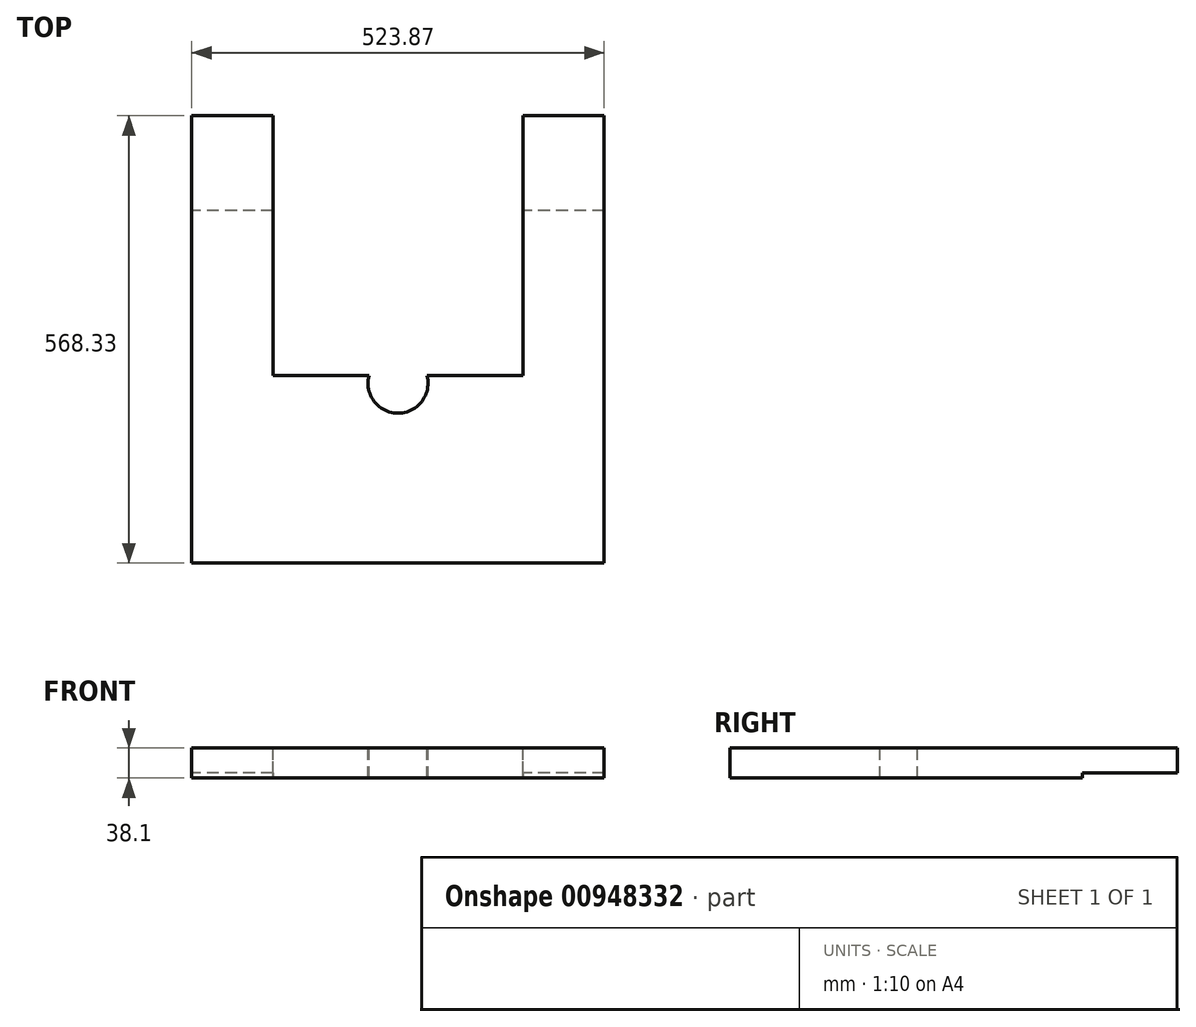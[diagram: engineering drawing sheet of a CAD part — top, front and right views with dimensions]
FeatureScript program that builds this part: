
annotation { "Feature Type Name" : "Feature", "Feature Type Description" : "" }
export const myFeature = defineFeature(function(context is Context, id is Id, definition is map)
    precondition{}
    {
        {
            var Q0;
            Q0=qCreatedBy(makeId("Top.planeOp"),FACE);
            var sketch = newSketch(context, id + "F0", { "sketchPlane" : qUnion([Q0])});
            skLineSegment(sketch, "E0.bottom", {"start": v(-267.02, 409.44) * mm, "end": v(256.85, 409.44) * mm});
            skLineSegment(sketch, "E0.top", {"start": v(-267.02, -158.89) * mm, "end": v(256.85, -158.89) * mm});
            skLineSegment(sketch, "E0.left", {"start": v(-267.02, 409.44) * mm, "end": v(-267.02, -158.89) * mm});
            skLineSegment(sketch, "E0.right", {"start": v(256.85, 409.44) * mm, "end": v(256.85, -158.89) * mm});
            skSolve(sketch);
        }
        {
            var Q0;
            Q0 = qSketchRegion(id + "F0", true);
            extrude(context, id + "F1", {"entities" : qUnion([Q0]), "depth" : 38.1 * mm, "offsetDistance" : 25.4 * mm});
        }
        {
            var Q0;
            Q0=makeQuery(id+"F1.opExtrude","CAP_FACE",FACE,{"disambiguationData":[OSD([sQuery(id+"F0.wireOp",EDGE,"E0.bottom"),sQuery(id+"F0.wireOp",EDGE,"E0.top"),sQuery(id+"F0.wireOp",EDGE,"E0.left"),sQuery(id+"F0.wireOp",EDGE,"E0.right")])],"isStart":false});
            var sketch = newSketch(context, id + "F2", { "sketchPlane" : qUnion([Q0])});
            skCircle(sketch, "E1", {"center": v(-5.09, 69.71) * mm, "radius": 38.1 * mm});
            skSolve(sketch);
        }
        {
            var Q0;
            Q0 = qSketchRegion(id + "F2", true);
            extrude(context, id + "F3", {"entities" : qUnion([Q0]), "operationType" : NewBodyOperationType.REMOVE, "oppositeDirection" : true, "depth" : 50.8 * mm, "offsetDistance" : 25.4 * mm});
        }
        {
            var Q0;
            Q0=makeQuery(id+"F1.opExtrude","CAP_FACE",FACE,{"disambiguationData":[OSD([sQuery(id+"F0.wireOp",EDGE,"E0.bottom"),sQuery(id+"F0.wireOp",EDGE,"E0.top"),sQuery(id+"F0.wireOp",EDGE,"E0.left"),sQuery(id+"F0.wireOp",EDGE,"E0.right")])],"isStart":false});
            var sketch = newSketch(context, id + "F4", { "sketchPlane" : qUnion([Q0])});
            skLineSegment(sketch, "E2.bottom", {"start": v(-163.84, 79.24) * mm, "end": v(153.66, 79.24) * mm});
            skLineSegment(sketch, "E2.top", {"start": v(-163.84, 409.44) * mm, "end": v(153.66, 409.44) * mm});
            skLineSegment(sketch, "E2.left", {"start": v(-163.84, 79.24) * mm, "end": v(-163.84, 409.44) * mm});
            skLineSegment(sketch, "E2.right", {"start": v(153.66, 79.24) * mm, "end": v(153.66, 409.44) * mm});
            skSolve(sketch);
        }
        {
            var Q0;
            Q0 = qSketchRegion(id + "F4", true);
            extrude(context, id + "F5", {"entities" : qUnion([Q0]), "operationType" : NewBodyOperationType.REMOVE, "oppositeDirection" : true, "depth" : 50.8 * mm, "offsetDistance" : 25.4 * mm});
        }
        {
            var Q0;
            Q0=makeQuery(id+"F1.opExtrude","CAP_FACE",FACE,{"disambiguationData":[OSD([sQuery(id+"F0.wireOp",EDGE,"E0.bottom"),sQuery(id+"F0.wireOp",EDGE,"E0.top"),sQuery(id+"F0.wireOp",EDGE,"E0.left"),sQuery(id+"F0.wireOp",EDGE,"E0.right")])],"isStart":true});
            var sketch = newSketch(context, id + "F6", { "sketchPlane" : qUnion([Q0])});
            skLineSegment(sketch, "E3.bottom", {"start": v(429.24, -409.44) * mm, "end": v(-466.81, -409.44) * mm});
            skLineSegment(sketch, "E3.top", {"start": v(429.24, -288.79) * mm, "end": v(-466.81, -288.79) * mm});
            skLineSegment(sketch, "E3.left", {"start": v(429.24, -409.44) * mm, "end": v(429.24, -288.79) * mm});
            skLineSegment(sketch, "E3.right", {"start": v(-466.81, -409.44) * mm, "end": v(-466.81, -288.79) * mm});
            skSolve(sketch);
        }
        {
            var Q0;
            Q0 = qSketchRegion(id + "F6", true);
            extrude(context, id + "F7", {"entities" : qUnion([Q0]), "operationType" : NewBodyOperationType.REMOVE, "oppositeDirection" : true, "depth" : 6.35 * mm, "offsetDistance" : 25.4 * mm});
        }
    });
